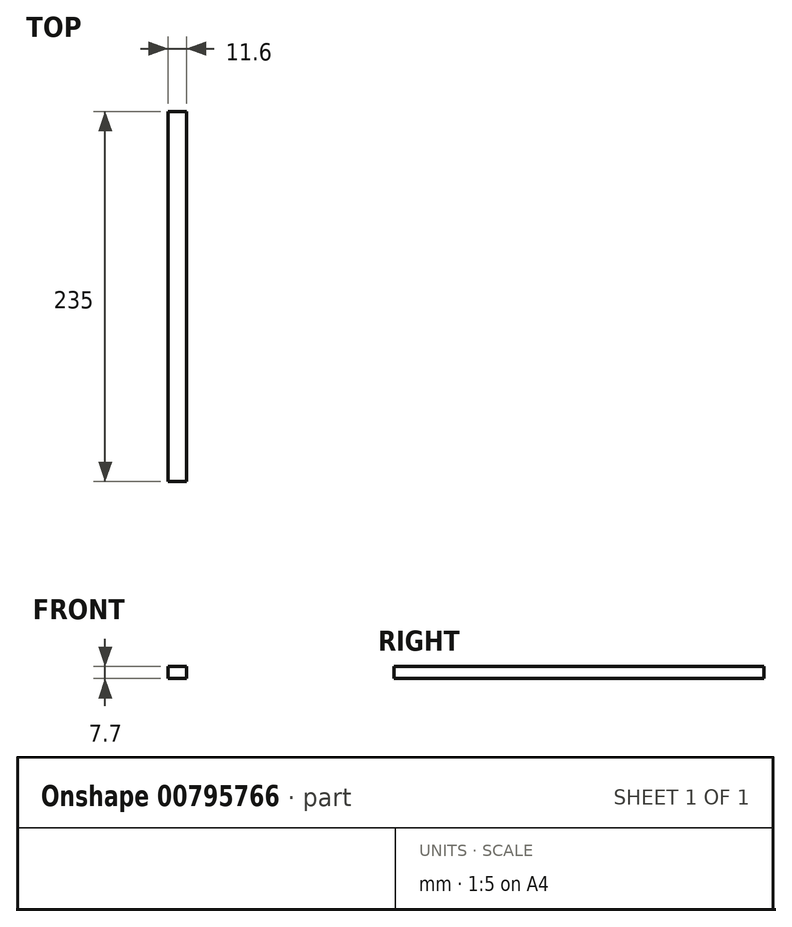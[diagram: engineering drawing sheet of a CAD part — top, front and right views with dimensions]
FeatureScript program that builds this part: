
annotation { "Feature Type Name" : "Feature", "Feature Type Description" : "" }
export const myFeature = defineFeature(function(context is Context, id is Id, definition is map)
    precondition{}
    {
        {
            var Q0;
            Q0=qCreatedBy(makeId("Front.planeOp"),FACE);
            var sketch = newSketch(context, id + "F0", { "sketchPlane" : qUnion([Q0])});
            skLineSegment(sketch, "E0.bottom", {"start": v(0, 0) * mm, "end": v(11.6, 0) * mm});
            skLineSegment(sketch, "E0.top", {"start": v(0, 7.7) * mm, "end": v(11.6, 7.7) * mm});
            skLineSegment(sketch, "E0.left", {"start": v(0, 0) * mm, "end": v(0, 7.7) * mm});
            skLineSegment(sketch, "E0.right", {"start": v(11.6, 0) * mm, "end": v(11.6, 7.7) * mm});
            skSolve(sketch);
        }
        {
            var Q0;
            Q0=makeQuery(id+"F0.imprint","IMPRINT",FACE,{"disambiguationData":[TD([[makeQuery(id+"F0.imprint","IMPRINT",EDGE,{"derivedFrom":sQuery(id+"F0.wireOp",EDGE,"E0.bottom")}),1.0]])]});
            extrude(context, id + "F1", {"entities" : qUnion([Q0]), "endBound" : BoundingType.SYMMETRIC, "depth" : 235 * mm, "offsetDistance" : 25 * mm});
        }
    });
